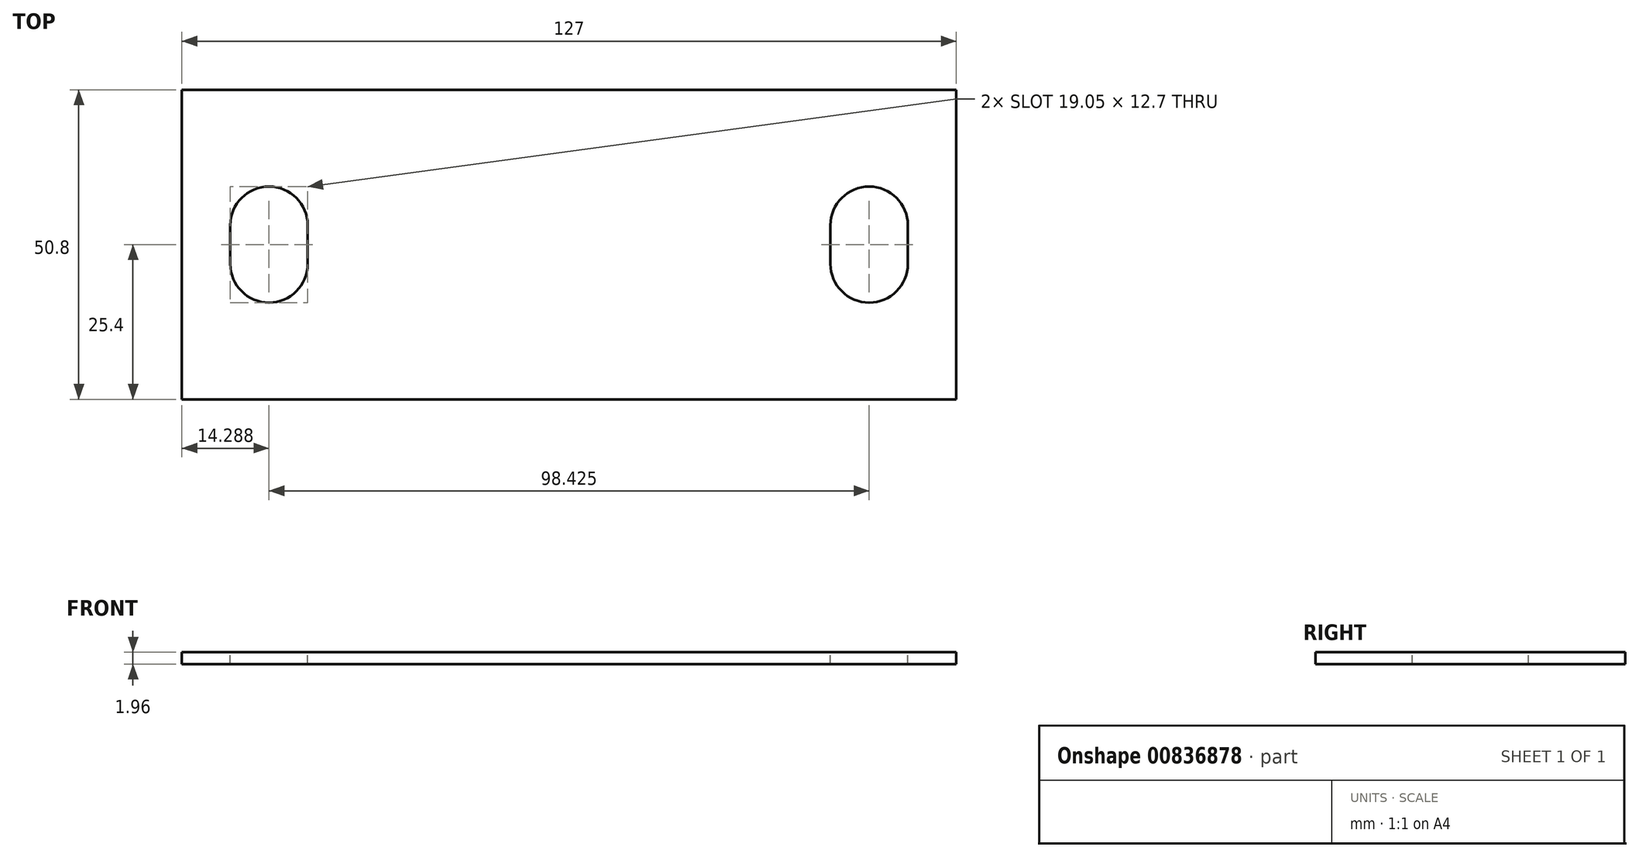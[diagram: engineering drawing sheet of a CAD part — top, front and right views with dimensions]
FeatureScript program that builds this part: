
annotation { "Feature Type Name" : "Feature", "Feature Type Description" : "" }
export const myFeature = defineFeature(function(context is Context, id is Id, definition is map)
    precondition{}
    {
        {
            var Q0;
            Q0=qCreatedBy(makeId("Front.planeOp"),FACE);
            var sketch = newSketch(context, id + "F0", { "sketchPlane" : qUnion([Q0])});
            skLineSegment(sketch, "E0.bottom", {"start": v(63.5, -0.98) * mm, "end": v(-63.5, -0.98) * mm});
            skLineSegment(sketch, "E0.top", {"start": v(63.5, 0.98) * mm, "end": v(-63.5, 0.98) * mm});
            skLineSegment(sketch, "E0.left", {"start": v(63.5, -0.98) * mm, "end": v(63.5, 0.98) * mm});
            skLineSegment(sketch, "E0.right", {"start": v(-63.5, -0.98) * mm, "end": v(-63.5, 0.98) * mm});
            skPoint(sketch, "E0.middle", {"position": v(0, 0) * mm});
            skSolve(sketch);
        }
        {
            var Q0;
            Q0 = qSketchRegion(id + "F0", true);
            extrude(context, id + "F1", {"entities" : qUnion([Q0]), "depth" : 50.8 * mm, "offsetDistance" : 25.4 * mm});
        }
        {
            var Q0;
            Q0=makeQuery(id+"F1.opExtrude","SWEPT_FACE",FACE,{"disambiguationData":[OSD([sQuery(id+"F0.wireOp",EDGE,"E0.top")])]});
            var sketch = newSketch(context, id + "F2", { "sketchPlane" : qUnion([Q0])});
            skLineSegment(sketch, "E1.bottom", {"start": v(-55.56, -22.23) * mm, "end": v(-42.86, -22.23) * mm, "construction": true});
            skLineSegment(sketch, "E1.top", {"start": v(-55.56, -28.58) * mm, "end": v(-42.86, -28.58) * mm, "construction": true});
            skLineSegment(sketch, "E1.left", {"start": v(-55.56, -22.23) * mm, "end": v(-55.56, -28.58) * mm});
            skLineSegment(sketch, "E1.right", {"start": v(-42.86, -22.23) * mm, "end": v(-42.86, -28.58) * mm});
            skArc(sketch, "E2", {"start": v(-42.86, -22.23) * mm, "mid": v(-49.21, -15.88) * mm, "end": v(-55.56, -22.23) * mm});
            skArc(sketch, "E3", {"start": v(-55.56, -28.58) * mm, "mid": v(-49.21, -34.93) * mm, "end": v(-42.86, -28.58) * mm});
            skLineSegment(sketch, "E4", {"start": v(-55.56, -25.4) * mm, "end": v(-42.86, -25.4) * mm, "construction": true});
            skLineSegment(sketch, "E5.MirrorCS", {"start": v(55.56, -22.23) * mm, "end": v(55.56, -28.58) * mm});
            skLineSegment(sketch, "E6.MirrorCS", {"start": v(42.86, -22.23) * mm, "end": v(42.86, -28.58) * mm});
            skArc(sketch, "E7.MirrorCS", {"start": v(42.86, -22.23) * mm, "mid": v(49.21, -15.88) * mm, "end": v(55.56, -22.23) * mm});
            skArc(sketch, "E8.MirrorCS", {"start": v(55.56, -28.58) * mm, "mid": v(49.21, -34.93) * mm, "end": v(42.86, -28.58) * mm});
            skLineSegment(sketch, "E9.MirrorCS", {"start": v(55.56, -28.58) * mm, "end": v(42.86, -28.58) * mm, "construction": true});
            skLineSegment(sketch, "E10.MirrorCS", {"start": v(55.56, -25.4) * mm, "end": v(42.86, -25.4) * mm, "construction": true});
            skLineSegment(sketch, "E11.MirrorCS", {"start": v(55.56, -22.23) * mm, "end": v(42.86, -22.23) * mm, "construction": true});
            skSolve(sketch);
        }
        {
            var Q0;
            Q0 = qSketchRegion(id + "F2", true);
            extrude(context, id + "F3", {"entities" : qUnion([Q0]), "operationType" : NewBodyOperationType.REMOVE, "oppositeDirection" : true, "depth" : 25.4 * mm, "offsetDistance" : 25.4 * mm});
        }
    });
